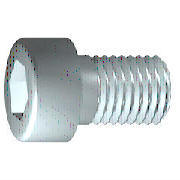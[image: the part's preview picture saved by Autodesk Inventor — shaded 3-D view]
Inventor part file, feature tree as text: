
AUTODESK INVENTOR PART (.ipt)
format: ipt  version: 2022 (Build 260153000, 153)  size: 199,168 bytes
history: native  units: mm (DEFAULTED — no unit token found)
features: sketch x2, extrude x1, plane x1, fillet x1
ambient origin geometry x7: Origin, YZ Plane, XY Plane, X Axis, Y Axis, Z Axis, Center Point
bodies: Solid1 (feature_tree), Body (feature_tree)
feature tree (5):
  extrude  "Slot"  Depth=3.0mm
  plane  "Work Plane1"
  fillet  "Fillet2"  Radius=3.0mm
  sketch  "Sketch1"  dims[d1=4.75mm d2=0.306825mm d3=3.0mm]
  sketch  "Sketch2"  dims[d4=1.3mm d5=60.0deg d6=3.0mm d7=3.0mm d8=2.886751mm d9=5.5mm d10=90.0deg d11=10.0mm d12=0.0mm d13=4.75mm d14=0.0mm d15=0.306725mm d16=0.306725mm d17=0.3mm d19=0.0mm d26=6.0mm d27=45.0deg d28=0.0mm d29=0.0mm d30=0.1mm]
